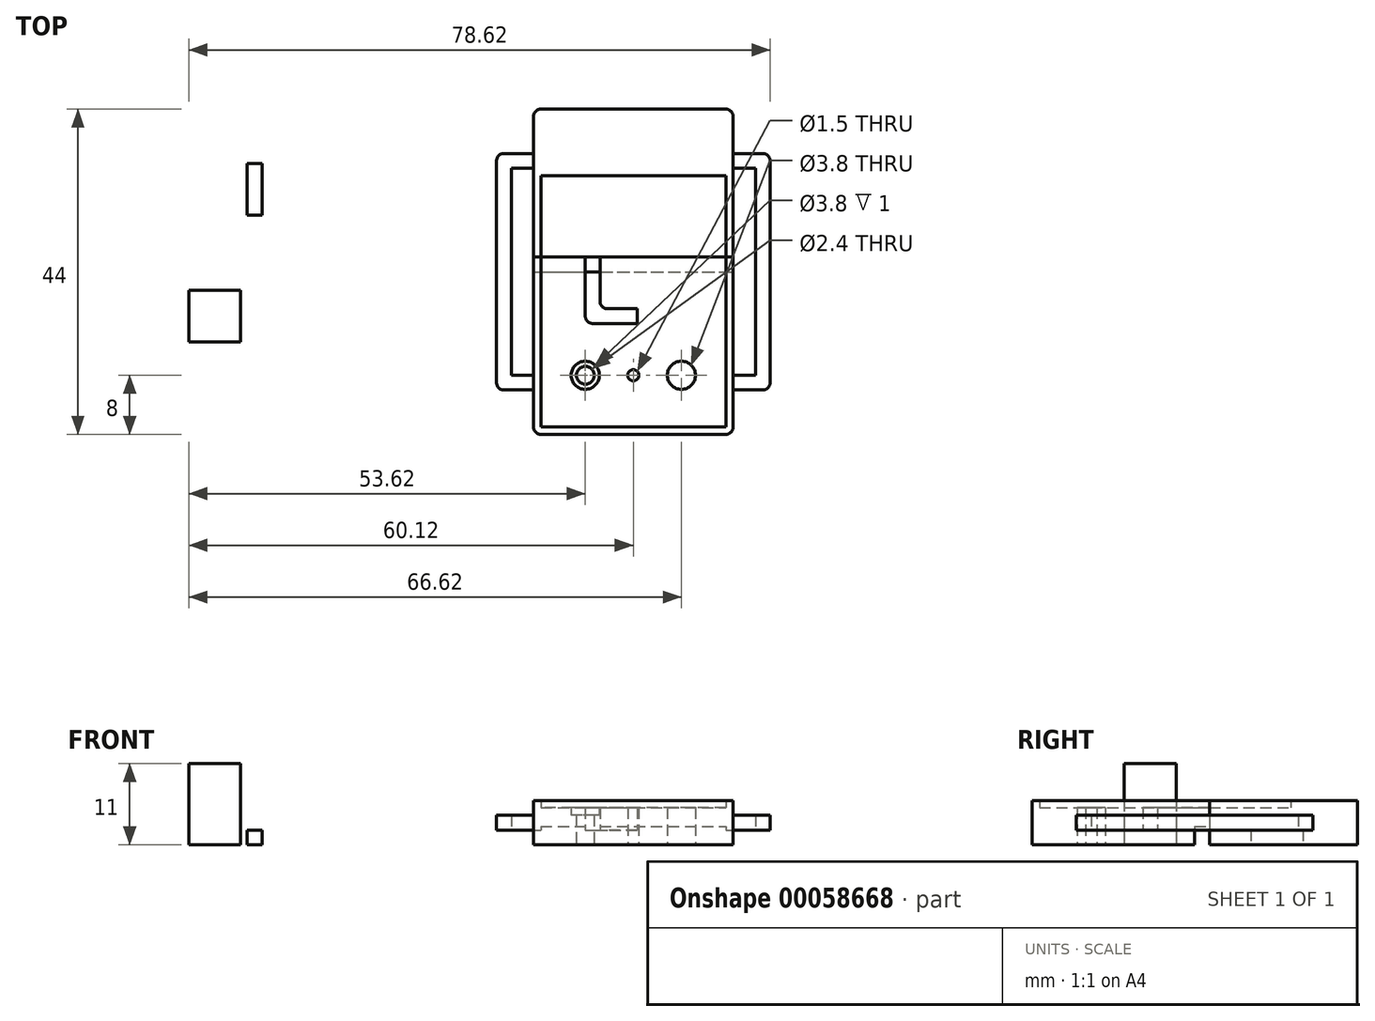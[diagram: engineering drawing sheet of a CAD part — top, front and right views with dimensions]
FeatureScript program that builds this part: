
annotation { "Feature Type Name" : "Feature", "Feature Type Description" : "" }
export const myFeature = defineFeature(function(context is Context, id is Id, definition is map)
    precondition{}
    {
        {
            var Q0;
            Q0=qCreatedBy(makeId("Top.planeOp"),FACE);
            var sketch = newSketch(context, id + "F0", { "sketchPlane" : qUnion([Q0])});
            skLineSegment(sketch, "E0", {"start": v(0, 0) * mm, "end": v(-12.5, 0) * mm});
            skLineSegment(sketch, "E1", {"start": v(-12.5, 0) * mm, "end": v(-12.5, 34) * mm});
            skLineSegment(sketch, "E2", {"start": v(-12.5, 34) * mm, "end": v(0, 34) * mm});
            skCircle(sketch, "E3", {"center": v(-6.5, 7) * mm, "radius": 1.9 * mm});
            skCircle(sketch, "E4", {"center": v(0, 7) * mm, "radius": 0.75 * mm});
            skLineSegment(sketch, "E5", {"start": v(-12.5, 43) * mm, "end": v(0, 43) * mm});
            skLineSegment(sketch, "E6", {"start": v(-13.5, 42) * mm, "end": v(-13.5, 35) * mm});
            skLineSegment(sketch, "E7", {"start": v(-12.5, -1) * mm, "end": v(0, -1) * mm});
            skLineSegment(sketch, "E8.MirrorCS", {"start": v(12.5, 43) * mm, "end": v(0, 43) * mm});
            skLineSegment(sketch, "E9.MirrorCS", {"start": v(13.5, 42) * mm, "end": v(13.5, 0) * mm});
            skLineSegment(sketch, "E10.MirrorCS", {"start": v(12.5, 34) * mm, "end": v(0, 34) * mm});
            skLineSegment(sketch, "E11.MirrorCS", {"start": v(12.5, 0) * mm, "end": v(12.5, 34) * mm});
            skLineSegment(sketch, "E12.MirrorCS", {"start": v(0, 0) * mm, "end": v(12.5, 0) * mm});
            skLineSegment(sketch, "E13.MirrorCS", {"start": v(12.5, -1) * mm, "end": v(0, -1) * mm});
            skCircle(sketch, "E14.MirrorC", {"center": v(6.5, 7) * mm, "radius": 1.9 * mm});
            skLineSegment(sketch, "E15", {"start": v(-13.5, 5) * mm, "end": v(-17.5, 5) * mm});
            skLineSegment(sketch, "E16", {"start": v(-18.5, 6) * mm, "end": v(-18.5, 36) * mm});
            skLineSegment(sketch, "E17", {"start": v(-17.5, 37) * mm, "end": v(-13.5, 37) * mm});
            skLineSegment(sketch, "E18", {"start": v(-13.5, 7) * mm, "end": v(-16.5, 7) * mm});
            skLineSegment(sketch, "E19", {"start": v(-16.5, 7) * mm, "end": v(-16.5, 35) * mm});
            skLineSegment(sketch, "E20", {"start": v(-16.5, 35) * mm, "end": v(-13.5, 35) * mm});
            skLineSegment(sketch, "E21.MirrorCS", {"start": v(17.5, 37) * mm, "end": v(13.5, 37) * mm});
            skLineSegment(sketch, "E22.MirrorCS", {"start": v(16.5, 35) * mm, "end": v(13.5, 35) * mm});
            skLineSegment(sketch, "E23.MirrorCS", {"start": v(16.5, 7) * mm, "end": v(16.5, 35) * mm});
            skLineSegment(sketch, "E24.MirrorCS", {"start": v(13.5, 5) * mm, "end": v(17.5, 5) * mm});
            skLineSegment(sketch, "E25.MirrorCS", {"start": v(13.5, 7) * mm, "end": v(16.5, 7) * mm});
            skLineSegment(sketch, "E26.MirrorCS", {"start": v(18.5, 6) * mm, "end": v(18.5, 36) * mm});
            skPoint(sketch, "E27.visualSharp", {"position": v(-18.5, 37) * mm});
            skArc(sketch, "E27.filletArc", {"start": v(-17.5, 37) * mm, "mid": v(-18.2, 36.7) * mm, "end": v(-18.5, 36) * mm});
            skPoint(sketch, "E28.visualSharp", {"position": v(-18.5, 5) * mm});
            skArc(sketch, "E28.filletArc", {"start": v(-18.5, 6) * mm, "mid": v(-18.2, 5.3) * mm, "end": v(-17.5, 5) * mm});
            skPoint(sketch, "E29.visualSharp", {"position": v(18.5, 5) * mm});
            skArc(sketch, "E29.filletArc", {"start": v(17.5, 5) * mm, "mid": v(18.2, 5.3) * mm, "end": v(18.5, 6) * mm});
            skPoint(sketch, "E30.visualSharp", {"position": v(18.5, 37) * mm});
            skArc(sketch, "E30.filletArc", {"start": v(18.5, 36) * mm, "mid": v(18.2, 36.7) * mm, "end": v(17.5, 37) * mm});
            skPoint(sketch, "E31.visualSharp", {"position": v(13.5, 43) * mm});
            skArc(sketch, "E31.filletArc", {"start": v(13.5, 42) * mm, "mid": v(13.2, 42.7) * mm, "end": v(12.5, 43) * mm});
            skPoint(sketch, "E32.visualSharp", {"position": v(-13.5, 43) * mm});
            skArc(sketch, "E32.filletArc", {"start": v(-12.5, 43) * mm, "mid": v(-13.2, 42.7) * mm, "end": v(-13.5, 42) * mm});
            skPoint(sketch, "E33.visualSharp", {"position": v(-13.5, -1) * mm});
            skArc(sketch, "E33.filletArc", {"start": v(-13.5, 0) * mm, "mid": v(-13.2, -0.7) * mm, "end": v(-12.5, -1) * mm});
            skPoint(sketch, "E34.visualSharp", {"position": v(13.5, -1) * mm});
            skArc(sketch, "E34.filletArc", {"start": v(12.5, -1) * mm, "mid": v(13.2, -0.7) * mm, "end": v(13.5, 0) * mm});
            skCircle(sketch, "E35", {"center": v(-6.5, 7) * mm, "radius": 1.2 * mm});
            skCircle(sketch, "E36.MirrorC", {"center": v(6.5, 7) * mm, "radius": 1.2 * mm});
            skLineSegment(sketch, "E37.trimOffspring", {"start": v(-13.5, 23) * mm, "end": v(-13.5, 0) * mm});
            skLineSegment(sketch, "E38", {"start": v(-13.5, 23) * mm, "end": v(-13.5, 35) * mm});
            skLineSegment(sketch, "E39", {"start": v(-13.5, 23) * mm, "end": v(13.5, 23) * mm});
            skLineSegment(sketch, "E40", {"start": v(-13.5, 21) * mm, "end": v(13.5, 21) * mm});
            skLineSegment(sketch, "E41", {"start": v(-6.5, 21) * mm, "end": v(-6.5, 15) * mm});
            skLineSegment(sketch, "E42", {"start": v(-5.5, 14) * mm, "end": v(-2.5, 14) * mm});
            skLineSegment(sketch, "E43", {"start": v(-4.5, 17) * mm, "end": v(-4.5, 21) * mm});
            skLineSegment(sketch, "E44", {"start": v(-2.5, 14) * mm, "end": v(0.5, 14) * mm});
            skLineSegment(sketch, "E45", {"start": v(0.5, 14) * mm, "end": v(0.5, 16) * mm});
            skLineSegment(sketch, "E46", {"start": v(0.5, 16) * mm, "end": v(-3.5, 16) * mm});
            skLineSegment(sketch, "E47", {"start": v(-6.5, 21) * mm, "end": v(-6.5, 23) * mm});
            skLineSegment(sketch, "E48", {"start": v(-4.5, 21) * mm, "end": v(-4.5, 23) * mm});
            skArc(sketch, "E49.filletArc", {"start": v(-4.5, 17) * mm, "mid": v(-4.2, 16.3) * mm, "end": v(-3.5, 16) * mm});
            skPoint(sketch, "E50.visualSharp", {"position": v(-6.5, 14) * mm});
            skArc(sketch, "E50.filletArc", {"start": v(-6.5, 15) * mm, "mid": v(-6.2, 14.3) * mm, "end": v(-5.5, 14) * mm});
            skSolve(sketch);
        }
        {
            var Q0;
            Q0=makeQuery(id+"F0.imprint","IMPRINT",FACE,{"disambiguationData":[TD([[makeQuery(id+"F0.imprint","IMPRINT",EDGE,{"derivedFrom":sQuery(id+"F0.wireOp",EDGE,"E0")}),1.0]])]});
            var Q1;
            {var subQ4=sQuery(id+"F0.wireOp",EDGE,"E2");Q1=makeQuery(id+"F0.imprint","IMPRINT",FACE,{"disambiguationData":[TD([[makeQuery(id+"F0.imprint","IMPRINT",EDGE,{"derivedFrom":subQ4}),1.0]])]});}
            extrude(context, id + "F1", {"entities" : qUnion([Q0, Q1]), "depth" : 6 * mm});
        }
        {
            var Q0;
            Q0=makeQuery(id+"F0.imprint","IMPRINT",FACE,{"disambiguationData":[TD([[makeQuery(id+"F0.imprint","IMPRINT",EDGE,{"derivedFrom":sQuery(id+"F0.wireOp",EDGE,"E0")}),-1.0]])]});
            var Q1;
            {var subQ6=sQuery(id+"F0.wireOp",EDGE,"E2");Q1=makeQuery(id+"F0.imprint","IMPRINT",FACE,{"disambiguationData":[TD([[makeQuery(id+"F0.imprint","IMPRINT",EDGE,{"derivedFrom":subQ6}),-1.0]])]});}
            extrude(context, id + "F2", {"entities" : qUnion([Q0, Q1]), "operationType" : NewBodyOperationType.ADD, "depth" : 5 * mm});
        }
        {
            var Q0;
            {var subQ2=sQuery(id+"F0.wireOp",EDGE,"E15");Q0=makeQuery(id+"F0.imprint","IMPRINT",FACE,{"disambiguationData":[TD([[makeQuery(id+"F0.imprint","IMPRINT",EDGE,{"derivedFrom":subQ2}),-1.0]])]});}
            var Q1;
            {var subQ4=sQuery(id+"F0.wireOp",EDGE,"E21.MirrorCS");Q1=makeQuery(id+"F0.imprint","IMPRINT",FACE,{"disambiguationData":[TD([[makeQuery(id+"F0.imprint","IMPRINT",EDGE,{"derivedFrom":subQ4}),1.0]])]});}
            extrude(context, id + "F3", {"entities" : qUnion([Q0, Q1]), "depth" : 4 * mm, "hasSecondDirection" : true, "secondDirectionOppositeDirection" : false, "secondDirectionDepth" : 2 * mm});
        }
        {
            var Q0;
            {var subQ0=sQuery(id+"F0.wireOp",EDGE,"E40");var subQ1=sQuery(id+"F0.wireOp",EDGE,"E1");var subQ2=makeQuery(id+"F0.imprint","INTERSECT",VERTEX,{"derivedFrom":[subQ1,subQ0]});Q0=makeQuery(id+"F0.imprint","IMPRINT",FACE,{"disambiguationData":[TD([[makeQuery(id+"F0.imprint","IMPRINT",EDGE,{"disambiguationData":[TD([[subQ2,-1.0]])],"derivedFrom":subQ1}),1.0]])]});}
            var Q1;
            {var subQ0=sQuery(id+"F0.wireOp",EDGE,"E39");var subQ1=sQuery(id+"F0.wireOp",EDGE,"E9.MirrorCS");var subQ2=makeQuery(id+"F0.imprint","INTERSECT",VERTEX,{"derivedFrom":[subQ1,subQ0]});Q1=makeQuery(id+"F0.imprint","IMPRINT",FACE,{"disambiguationData":[TD([[makeQuery(id+"F0.imprint","IMPRINT",EDGE,{"disambiguationData":[TD([[subQ2,-1.0]])],"derivedFrom":subQ1}),-1.0]])]});}
            extrude(context, id + "F4", {"entities" : qUnion([Q0, Q1]), "depth" : 6 * mm, "hasSecondDirection" : true, "secondDirectionOppositeDirection" : false, "secondDirectionDepth" : 2 * mm});
        }
        {
            var Q0;
            {var subQ0=sQuery(id+"F0.wireOp",EDGE,"E40");var subQ2=sQuery(id+"F0.wireOp",EDGE,"E1");var subQ3=makeQuery(id+"F0.imprint","INTERSECT",VERTEX,{"derivedFrom":[subQ2,subQ0]});Q0=makeQuery(id+"F0.imprint","IMPRINT",FACE,{"disambiguationData":[TD([[makeQuery(id+"F0.imprint","IMPRINT",EDGE,{"disambiguationData":[TD([[subQ3,-1.0]])],"derivedFrom":subQ2}),-1.0]])]});}
            var Q1;
            {var subQ5=sQuery(id+"F0.wireOp",EDGE,"E48");Q1=makeQuery(id+"F0.imprint","IMPRINT",FACE,{"disambiguationData":[TD([[makeQuery(id+"F0.imprint","IMPRINT",EDGE,{"derivedFrom":subQ5}),-1.0]])]});}
            extrude(context, id + "F5", {"entities" : qUnion([Q0, Q1]), "depth" : 5 * mm, "hasSecondDirection" : true, "secondDirectionOppositeDirection" : false, "secondDirectionDepth" : 2.5 * mm});
        }
        {
            var Q0;
            {var subQ3=sQuery(id+"F0.wireOp",EDGE,"E41");Q0=makeQuery(id+"F0.imprint","IMPRINT",FACE,{"disambiguationData":[TD([[makeQuery(id+"F0.imprint","IMPRINT",EDGE,{"derivedFrom":subQ3}),1.0]])]});}
            var Q1;
            {var subQ0=sQuery(id+"F0.wireOp",EDGE,"E44");Q1=makeQuery(id+"F0.imprint","IMPRINT",FACE,{"disambiguationData":[TD([[makeQuery(id+"F0.imprint","IMPRINT",EDGE,{"derivedFrom":subQ0}),1.0]])]});}
            extrude(context, id + "F6", {"entities" : qUnion([Q0, Q1]), "depth" : 2 * mm});
        }
        {
            var Q0;
            Q0=makeQuery(id+"F0.imprint","IMPRINT",FACE,{"disambiguationData":[TD([[makeQuery(id+"F0.imprint","IMPRINT",EDGE,{"derivedFrom":sQuery(id+"F0.wireOp",EDGE,"E3")}),1.0]])]});
            var Q1;
            Q1=makeQuery(id+"F0.imprint","IMPRINT",FACE,{"disambiguationData":[TD([[makeQuery(id+"F0.imprint","IMPRINT",EDGE,{"derivedFrom":sQuery(id+"F0.wireOp",EDGE,"E14.MirrorC")}),-1.0]])]});
            extrude(context, id + "F7", {"entities" : qUnion([Q0, Q1]), "operationType" : NewBodyOperationType.ADD, "depth" : 4 * mm});
        }
        {
            var Q0;
            Q0=qCreatedBy(makeId("Top.planeOp"),FACE);
            var sketch = newSketch(context, id + "F8", { "sketchPlane" : qUnion([Q0])});
            skLineSegment(sketch, "E51.bottom", {"start": v(-52.22, 35.63) * mm, "end": v(-50.22, 35.63) * mm});
            skLineSegment(sketch, "E51.top", {"start": v(-52.22, 28.63) * mm, "end": v(-50.22, 28.63) * mm});
            skLineSegment(sketch, "E51.left", {"start": v(-52.22, 35.63) * mm, "end": v(-52.22, 28.63) * mm});
            skLineSegment(sketch, "E51.right", {"start": v(-50.22, 35.63) * mm, "end": v(-50.22, 28.63) * mm});
            skLineSegment(sketch, "E52.rect.bottom", {"start": v(-53.12, 11.5) * mm, "end": v(-60.12, 11.5) * mm});
            skLineSegment(sketch, "E52.rect.top", {"start": v(-53.12, 18.5) * mm, "end": v(-60.12, 18.5) * mm});
            skLineSegment(sketch, "E52.rect.left", {"start": v(-53.12, 11.5) * mm, "end": v(-53.12, 18.5) * mm});
            skLineSegment(sketch, "E52.rect.right", {"start": v(-60.12, 11.5) * mm, "end": v(-60.12, 18.5) * mm});
            skPoint(sketch, "E52.rect.middle", {"position": v(-56.62, 15) * mm});
            skSolve(sketch);
        }
        {
            var Q0;
            Q0=qSketchRegion(id+"F8",true);
            var Q1;
            Q1=makeQuery(id+"F8.imprint","IMPRINT",FACE,{"disambiguationData":[TD([[makeQuery(id+"F8.imprint","IMPRINT",EDGE,{"derivedFrom":sQuery(id+"F8.wireOp",EDGE,"E51.bottom")}),-1.0]])]});
            extrude(context, id + "F9", {"entities" : qUnion([Q0, Q1]), "depth" : 2 * mm});
        }
        {
            var Q0;
            Q0=makeQuery(id+"F9.opExtrude","CAP_FACE",FACE,{"disambiguationData":[OSD([sQuery(id+"F8.wireOp",EDGE,"E52.rect.bottom"),sQuery(id+"F8.wireOp",EDGE,"E52.rect.top"),sQuery(id+"F8.wireOp",EDGE,"E52.rect.left"),sQuery(id+"F8.wireOp",EDGE,"E52.rect.right")])],"isStart":false});
            extrude(context, id + "F10", {"entities" : qUnion([Q0]), "operationType" : NewBodyOperationType.ADD, "depth" : 9 * mm});
        }
    });
